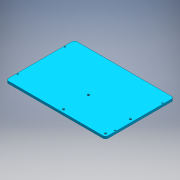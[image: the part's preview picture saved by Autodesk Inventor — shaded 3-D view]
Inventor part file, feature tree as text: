
AUTODESK INVENTOR PART (.ipt)
format: ipt  version: 2016 (Build 200138000, 138)  size: 134,144 bytes
history: native  units: mm
features: sketch x3, hole x2, extrude x1
ambient origin geometry x8: Origin, YZ Plane, XZ Plane, XY Plane, X Axis, Y Axis, Z Axis, Center Point
bodies: Solid1 (feature_tree)
feature tree (6):
  extrude  "Extrusion1"  Depth=110.0mm
  hole  "Hole1"  [1 undecoded]
  hole  "Hole2"  [1 undecoded]
  sketch  "Sketch1"  dims[d0=160.0mm d1=110.0mm]
  sketch  "Sketch2"  dims[d2=55.0mm d3=80.0mm]
  sketch  "Sketch3"  dims[d4=4.0mm d5=3.75mm d6=0.0mm d7=156.6mm d8=76.0mm d9=38.0mm d10=78.3mm d11=2.013mm d12=5.0mm d13=11.0mm d14=2.6mm d15=14.3117mm d16=7.6mm d17=20.594885mm d18=40.0mm d19=67.5mm d20=5.0mm d21=5.0mm d22=3.242mm d23=8.0mm d24=11.0mm d25=2.6mm d26=14.3117mm d27=11.8mm d28=20.594885mm]
note: 2 required parameter values undecoded (feature->parameter linkage not recoverable at this tier; creation-order binding heuristic only, values carry confidence <= 0.55)
